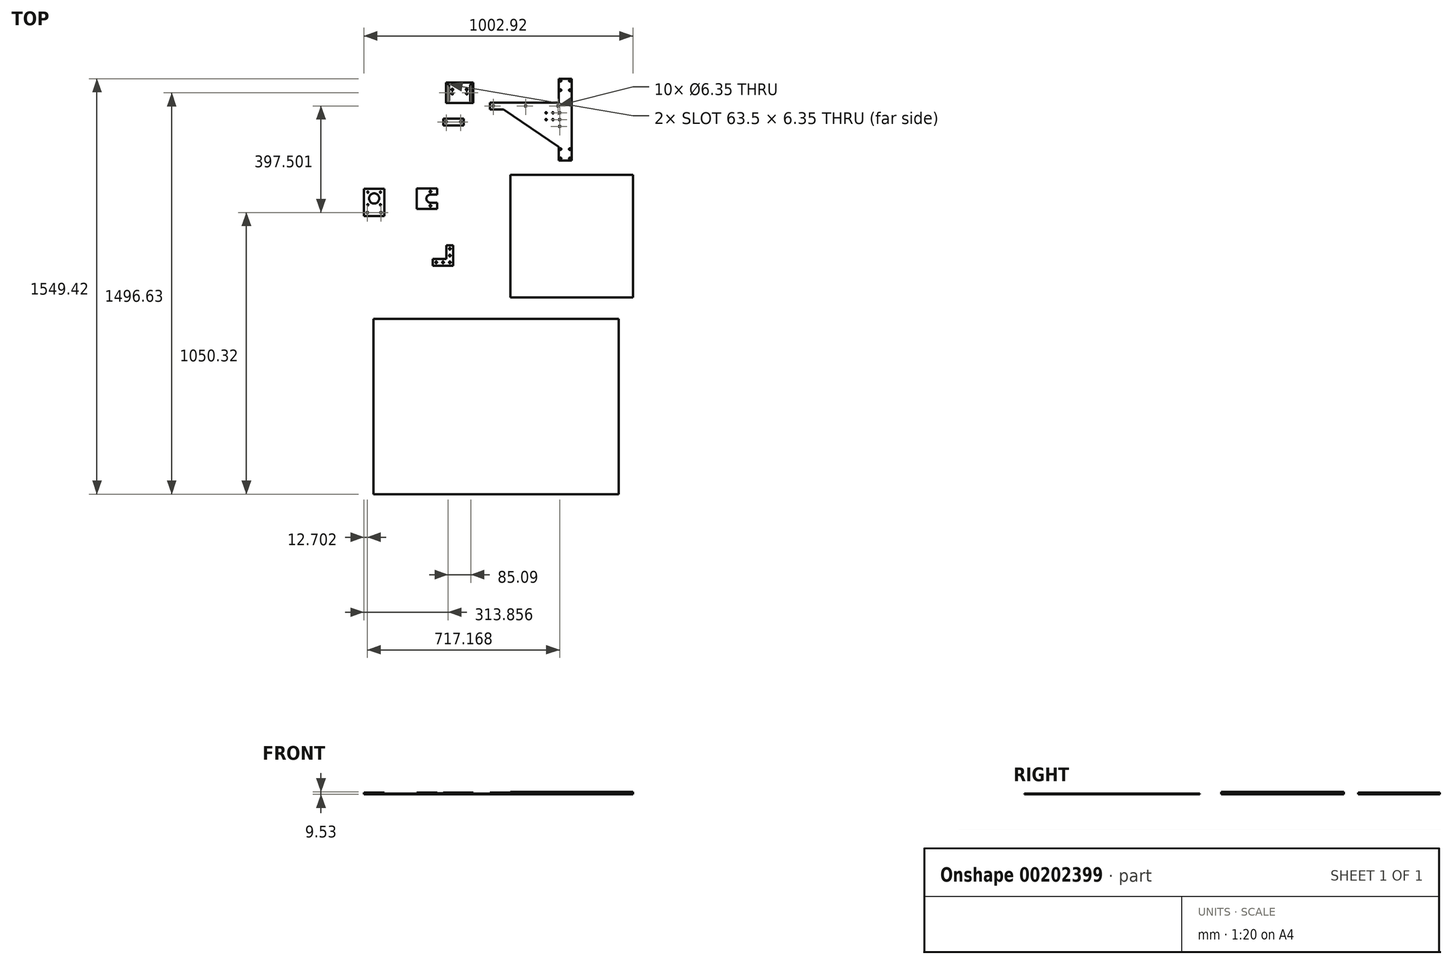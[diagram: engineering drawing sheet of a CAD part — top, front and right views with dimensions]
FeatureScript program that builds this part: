
annotation { "Feature Type Name" : "Feature", "Feature Type Description" : "" }
export const myFeature = defineFeature(function(context is Context, id is Id, definition is map)
    precondition{}
    {
        {
            var Q0;
            Q0=qCreatedBy(makeId("Top.planeOp"),FACE);
            var sketch = newSketch(context, id + "F0", { "sketchPlane" : qUnion([Q0])});
            skLineSegment(sketch, "E0.rect.bottom", {"start": v(228.6, 228.6) * mm, "end": v(-228.6, 228.6) * mm});
            skLineSegment(sketch, "E0.rect.top", {"start": v(228.6, -228.6) * mm, "end": v(-228.6, -228.6) * mm});
            skLineSegment(sketch, "E0.rect.left", {"start": v(228.6, 228.6) * mm, "end": v(228.6, -228.6) * mm});
            skLineSegment(sketch, "E0.rect.right", {"start": v(-228.6, 228.6) * mm, "end": v(-228.6, -228.6) * mm});
            skPoint(sketch, "E0.rect.middle", {"position": v(0, 0) * mm});
            skSolve(sketch);
        }
        {
            var Q0;
            Q0=makeQuery(id+"F0.imprint","IMPRINT",FACE,{"disambiguationData":[TD([[makeQuery(id+"F0.imprint","IMPRINT",EDGE,{"derivedFrom":sQuery(id+"F0.wireOp",EDGE,"E0.rect.bottom")}),1.0]])]});
            extrude(context, id + "F1", {"entities" : qUnion([Q0]), "depth" : 9.52 * mm});
        }
        {
            var Q0;
            Q0=qCreatedBy(makeId("Top.planeOp"),FACE);
            var sketch = newSketch(context, id + "F2", { "sketchPlane" : qUnion([Q0])});
            skLineSegment(sketch, "E1.rect.left", {"start": v(0, 281.9) * mm, "end": v(0, 586.7) * mm});
            skLineSegment(sketch, "E2", {"start": v(-47.75, 281.9) * mm, "end": v(0, 281.9) * mm});
            skLineSegment(sketch, "E3", {"start": v(-47.75, 586.7) * mm, "end": v(0, 586.7) * mm});
            skLineSegment(sketch, "E4", {"start": v(-304.8, 497.8) * mm, "end": v(-304.8, 472.4) * mm});
            skLineSegment(sketch, "E5", {"start": v(-47.75, 281.9) * mm, "end": v(-47.75, 332.7) * mm});
            skLineSegment(sketch, "E6", {"start": v(-47.75, 586.7) * mm, "end": v(-47.75, 497.8) * mm});
            skLineSegment(sketch, "E7", {"start": v(-304.8, 497.8) * mm, "end": v(-254, 497.8) * mm});
            skLineSegment(sketch, "E8", {"start": v(-254, 497.8) * mm, "end": v(-47.75, 497.8) * mm});
            skLineSegment(sketch, "E9", {"start": v(-304.8, 472.4) * mm, "end": v(-254, 472.4) * mm});
            skLineSegment(sketch, "E10", {"start": v(-254, 472.4) * mm, "end": v(-47.75, 332.7) * mm});
            skLineSegment(sketch, "E11", {"start": v(-304.8, 485.1) * mm, "end": v(0, 485.1) * mm, "construction": true});
            skLineSegment(sketch, "E12", {"start": v(-41.38, 586.7) * mm, "end": v(-41.38, 579.19) * mm, "construction": true});
            skLineSegment(sketch, "E13", {"start": v(-6.38, 586.7) * mm, "end": v(-6.38, 281.9) * mm, "construction": true});
            skLineSegment(sketch, "E14", {"start": v(-47.75, 579.19) * mm, "end": v(0, 579.19) * mm, "construction": true});
            skLineSegment(sketch, "E15", {"start": v(-47.75, 544.19) * mm, "end": v(0, 544.19) * mm, "construction": true});
            skLineSegment(sketch, "E16", {"start": v(-47.75, 324.43) * mm, "end": v(0, 324.43) * mm, "construction": true});
            skLineSegment(sketch, "E17", {"start": v(-47.75, 289.43) * mm, "end": v(-41.38, 289.43) * mm, "construction": true});
            skLineSegment(sketch, "E18", {"start": v(-41.38, 324.43) * mm, "end": v(-41.38, 289.43) * mm, "construction": true});
            skLineSegment(sketch, "E19", {"start": v(-41.38, 289.43) * mm, "end": v(-41.38, 281.9) * mm, "construction": true});
            skLineSegment(sketch, "E20", {"start": v(-41.38, 289.43) * mm, "end": v(-6.38, 289.43) * mm, "construction": true});
            skLineSegment(sketch, "E21", {"start": v(-6.38, 289.43) * mm, "end": v(0, 289.43) * mm, "construction": true});
            skLineSegment(sketch, "E22", {"start": v(-41.38, 579.19) * mm, "end": v(-41.38, 544.19) * mm, "construction": true});
            skLineSegment(sketch, "E23", {"start": v(-41.38, 544.19) * mm, "end": v(-41.38, 324.43) * mm, "construction": true});
            skPoint(sketch, "E24", {"position": v(-41.38, 306.93) * mm});
            skPoint(sketch, "E25", {"position": v(-41.38, 561.69) * mm});
            skCircle(sketch, "E26", {"center": v(-41.38, 324.43) * mm, "radius": 3.2 * mm});
            skCircle(sketch, "E27", {"center": v(-6.38, 324.43) * mm, "radius": 3.2 * mm});
            skCircle(sketch, "E28", {"center": v(-41.38, 289.43) * mm, "radius": 3.2 * mm});
            skCircle(sketch, "E29", {"center": v(-6.38, 289.43) * mm, "radius": 3.2 * mm});
            skCircle(sketch, "E30", {"center": v(-41.38, 579.19) * mm, "radius": 3.2 * mm});
            skCircle(sketch, "E31", {"center": v(-6.38, 579.19) * mm, "radius": 3.2 * mm});
            skCircle(sketch, "E32", {"center": v(-41.38, 544.19) * mm, "radius": 3.2 * mm});
            skCircle(sketch, "E33", {"center": v(-6.38, 544.19) * mm, "radius": 3.2 * mm});
            skCircle(sketch, "E34", {"center": v(-171.45, 485.1) * mm, "radius": 3.17 * mm});
            skCircle(sketch, "E35", {"center": v(-50.8, 485.1) * mm, "radius": 3.17 * mm});
            skCircle(sketch, "E36", {"center": v(-292.1, 485.1) * mm, "radius": 3.17 * mm});
            skCircle(sketch, "E37", {"center": v(-69.85, 459.7) * mm, "radius": 2.55 * mm});
            skCircle(sketch, "E38", {"center": v(-69.85, 434.3) * mm, "radius": 2.55 * mm});
            skCircle(sketch, "E39", {"center": v(-95.25, 459.7) * mm, "radius": 2.55 * mm});
            skCircle(sketch, "E40", {"center": v(-95.25, 434.3) * mm, "radius": 2.55 * mm});
            skLineSegment(sketch, "E41", {"start": v(-44.45, 608.23) * mm, "end": v(-44.45, 265.2) * mm, "construction": true});
            skCircle(sketch, "E42", {"center": v(-44.45, 459.7) * mm, "radius": 3.17 * mm});
            skCircle(sketch, "E43", {"center": v(-44.45, 434.3) * mm, "radius": 3.17 * mm});
            skCircle(sketch, "E44", {"center": v(-44.45, 408.9) * mm, "radius": 3.18 * mm});
            skSolve(sketch);
        }
        {
            var Q0;
            Q0=makeQuery(id+"F2.imprint","IMPRINT",FACE,{"disambiguationData":[TD([[makeQuery(id+"F2.imprint","IMPRINT",EDGE,{"derivedFrom":sQuery(id+"F2.wireOp",EDGE,"E1.rect.left")}),1.0]])]});
            extrude(context, id + "F3", {"entities" : qUnion([Q0]), "depth" : 6.35 * mm});
        }
        {
            var Q0;
            Q0=qCreatedBy(makeId("Top.planeOp"),FACE);
            var sketch = newSketch(context, id + "F4", { "sketchPlane" : qUnion([Q0])});
            skLineSegment(sketch, "E45", {"start": v(-517.53, -110.74) * mm, "end": v(-441.33, -110.74) * mm});
            skLineSegment(sketch, "E46", {"start": v(-441.33, -110.74) * mm, "end": v(-441.33, -34.54) * mm});
            skLineSegment(sketch, "E47", {"start": v(-441.33, -34.54) * mm, "end": v(-466.73, -34.54) * mm});
            skLineSegment(sketch, "E48", {"start": v(-466.73, -34.54) * mm, "end": v(-466.73, -85.34) * mm});
            skLineSegment(sketch, "E49", {"start": v(-466.73, -85.34) * mm, "end": v(-517.53, -85.34) * mm});
            skLineSegment(sketch, "E50", {"start": v(-517.53, -85.34) * mm, "end": v(-517.53, -110.74) * mm});
            skCircle(sketch, "E51", {"center": v(-454.03, -98.04) * mm, "radius": 3.26 * mm});
            skCircle(sketch, "E52.1.0.0", {"center": v(-454.03, -72.64) * mm, "radius": 3.26 * mm});
            skCircle(sketch, "E52.2.0.0", {"center": v(-454.03, -47.24) * mm, "radius": 3.26 * mm});
            skLineSegment(sketch, "E52.direction1", {"start": v(-454.03, -98.04) * mm, "end": v(-454.03, -72.64) * mm, "construction": true});
            skCircle(sketch, "E53.1.0.0", {"center": v(-479.43, -98.04) * mm, "radius": 3.26 * mm});
            skCircle(sketch, "E53.2.0.0", {"center": v(-504.83, -98.04) * mm, "radius": 3.26 * mm});
            skLineSegment(sketch, "E53.direction1", {"start": v(-454.03, -98.04) * mm, "end": v(-479.43, -98.04) * mm, "construction": true});
            skSolve(sketch);
        }
        {
            var Q0;
            Q0=makeQuery(id+"F4.imprint","IMPRINT",FACE,{"disambiguationData":[TD([[makeQuery(id+"F4.imprint","IMPRINT",EDGE,{"derivedFrom":sQuery(id+"F4.wireOp",EDGE,"E45")}),1.0]])]});
            extrude(context, id + "F5", {"entities" : qUnion([Q0]), "depth" : 4.78 * mm});
        }
        {
            var Q0;
            Q0=qCreatedBy(makeId("Top.planeOp"),FACE);
            var sketch = newSketch(context, id + "F6", { "sketchPlane" : qUnion([Q0])});
            skLineSegment(sketch, "E54.bottom", {"start": v(-577.32, 177.55) * mm, "end": v(-526.52, 177.55) * mm});
            skLineSegment(sketch, "E54.top", {"start": v(-577.32, 101.35) * mm, "end": v(-526.52, 101.35) * mm});
            skLineSegment(sketch, "E54.left", {"start": v(-577.32, 177.55) * mm, "end": v(-577.32, 101.35) * mm});
            skLineSegment(sketch, "E54.right", {"start": v(-526.52, 177.55) * mm, "end": v(-526.52, 154.45) * mm, "construction": true});
            skArc(sketch, "E55", {"start": v(-526.52, 154.45) * mm, "mid": v(-541.52, 139.45) * mm, "end": v(-526.52, 124.45) * mm});
            skLineSegment(sketch, "E56.trimOffspring", {"start": v(-526.52, 124.45) * mm, "end": v(-526.52, 101.35) * mm, "construction": true});
            skLineSegment(sketch, "E57", {"start": v(-526.52, 101.35) * mm, "end": v(-501.12, 101.35) * mm});
            skLineSegment(sketch, "E58", {"start": v(-501.12, 101.35) * mm, "end": v(-501.12, 124.45) * mm});
            skLineSegment(sketch, "E59", {"start": v(-501.12, 124.45) * mm, "end": v(-526.52, 124.45) * mm});
            skLineSegment(sketch, "E60", {"start": v(-526.52, 154.45) * mm, "end": v(-501.12, 154.45) * mm});
            skLineSegment(sketch, "E61", {"start": v(-501.12, 154.45) * mm, "end": v(-501.12, 177.55) * mm});
            skLineSegment(sketch, "E62", {"start": v(-501.12, 177.55) * mm, "end": v(-526.52, 177.55) * mm});
            skCircle(sketch, "E63", {"center": v(-526.52, 166) * mm, "radius": 3.3 * mm});
            skCircle(sketch, "E64", {"center": v(-526.52, 112.9) * mm, "radius": 3.3 * mm});
            skSolve(sketch);
        }
        {
            var Q0;
            Q0=makeQuery(id+"F6.imprint","IMPRINT",FACE,{"disambiguationData":[TD([[makeQuery(id+"F6.imprint","IMPRINT",EDGE,{"derivedFrom":sQuery(id+"F6.wireOp",EDGE,"E54.bottom")}),-1.0]])]});
            extrude(context, id + "F7", {"entities" : qUnion([Q0]), "depth" : 6.35 * mm});
        }
        {
            var Q0;
            Q0=qCreatedBy(makeId("Top.planeOp"),FACE);
            var sketch = newSketch(context, id + "F8", { "sketchPlane" : qUnion([Q0])});
            skLineSegment(sketch, "E65.rect.bottom", {"start": v(175.27, -962.71) * mm, "end": v(-739.13, -962.71) * mm});
            skLineSegment(sketch, "E65.rect.top", {"start": v(175.27, -308.66) * mm, "end": v(-739.13, -308.66) * mm});
            skLineSegment(sketch, "E65.rect.left", {"start": v(175.27, -962.71) * mm, "end": v(175.27, -308.66) * mm});
            skLineSegment(sketch, "E65.rect.right", {"start": v(-739.13, -962.71) * mm, "end": v(-739.13, -308.66) * mm});
            skPoint(sketch, "E65.rect.middle", {"position": v(-281.93, -635.69) * mm});
            skSolve(sketch);
        }
        {
            var Q0;
            Q0=makeQuery(id+"F8.imprint","IMPRINT",FACE,{"disambiguationData":[TD([[makeQuery(id+"F8.imprint","IMPRINT",EDGE,{"derivedFrom":sQuery(id+"F8.wireOp",EDGE,"E65.rect.bottom")}),-1.0]])]});
            extrude(context, id + "F9", {"entities" : qUnion([Q0]), "depth" : 3.17 * mm});
        }
        {
            var Q0;
            Q0=makeQuery(id+"F1.opExtrude","CAP_FACE",FACE,{"disambiguationData":[OSD([sQuery(id+"F0.wireOp",EDGE,"E0.rect.bottom"),sQuery(id+"F0.wireOp",EDGE,"E0.rect.top"),sQuery(id+"F0.wireOp",EDGE,"E0.rect.left"),sQuery(id+"F0.wireOp",EDGE,"E0.rect.right")])],"isStart":true});
            var sketch = newSketch(context, id + "F10", { "sketchPlane" : qUnion([Q0])});
            skLineSegment(sketch, "E66", {"start": v(0, 177.8) * mm, "end": v(152.4, 177.8) * mm, "construction": true});
            skLineSegment(sketch, "E67", {"start": v(76.2, 59.27) * mm, "end": v(-76.2, 59.27) * mm, "construction": true});
            skLineSegment(sketch, "E68", {"start": v(-152.4, -59.27) * mm, "end": v(152.4, -59.27) * mm, "construction": true});
            skLineSegment(sketch, "E69", {"start": v(76.2, -177.8) * mm, "end": v(-76.2, -177.8) * mm, "construction": true});
            skLineSegment(sketch, "E70", {"start": v(76.2, -177.8) * mm, "end": v(76.2, -59.27) * mm, "construction": true});
            skLineSegment(sketch, "E71", {"start": v(76.2, -59.27) * mm, "end": v(76.2, 59.27) * mm, "construction": true});
            skLineSegment(sketch, "E72", {"start": v(76.2, 59.27) * mm, "end": v(76.2, 177.8) * mm, "construction": true});
            skPoint(sketch, "E73", {"position": v(0, 177.8) * mm});
            skPoint(sketch, "E74", {"position": v(0, -59.27) * mm});
            skLineSegment(sketch, "E75", {"start": v(76.2, 177.8) * mm, "end": v(76.2, 228.6) * mm, "construction": true});
            skLineSegment(sketch, "E76", {"start": v(76.2, -177.8) * mm, "end": v(76.2, -228.6) * mm, "construction": true});
            skLineSegment(sketch, "E77", {"start": v(-152.4, 177.8) * mm, "end": v(-228.6, 177.8) * mm, "construction": true});
            skLineSegment(sketch, "E78", {"start": v(-76.2, 59.27) * mm, "end": v(-228.6, 59.27) * mm, "construction": true});
            skLineSegment(sketch, "E79", {"start": v(152.4, 177.8) * mm, "end": v(228.6, 177.8) * mm, "construction": true});
            skLineSegment(sketch, "E80", {"start": v(76.2, 59.27) * mm, "end": v(228.6, 59.27) * mm, "construction": true});
            skLineSegment(sketch, "E81", {"start": v(-152.4, 177.8) * mm, "end": v(0, 177.8) * mm, "construction": true});
            skSolve(sketch);
        }
        {
            var Q0;
            Q0=qCreatedBy(makeId("Top.planeOp"),FACE);
            var sketch = newSketch(context, id + "F11", { "sketchPlane" : qUnion([Q0])});
            skLineSegment(sketch, "E82.bottom", {"start": v(-468.72, 572.02) * mm, "end": v(-367.12, 572.02) * mm});
            skLineSegment(sketch, "E82.top", {"start": v(-468.72, 495.82) * mm, "end": v(-367.12, 495.82) * mm});
            skLineSegment(sketch, "E82.left", {"start": v(-468.72, 572.02) * mm, "end": v(-468.72, 495.82) * mm});
            skLineSegment(sketch, "E82.right", {"start": v(-367.12, 572.02) * mm, "end": v(-367.12, 495.82) * mm});
            skLineSegment(sketch, "E83.bottom", {"start": v(-478.47, 438.44) * mm, "end": v(-402.27, 438.44) * mm});
            skLineSegment(sketch, "E83.top", {"start": v(-478.47, 413.04) * mm, "end": v(-402.27, 413.04) * mm});
            skLineSegment(sketch, "E83.left", {"start": v(-478.47, 438.44) * mm, "end": v(-478.47, 413.04) * mm});
            skLineSegment(sketch, "E83.right", {"start": v(-402.27, 438.44) * mm, "end": v(-402.27, 413.04) * mm});
            skLineSegment(sketch, "E84", {"start": v(-478.47, 425.74) * mm, "end": v(-467.37, 425.74) * mm, "construction": true});
            skLineSegment(sketch, "E85", {"start": v(-468.72, 546.62) * mm, "end": v(-444.92, 546.62) * mm, "construction": true});
            skLineSegment(sketch, "E86", {"start": v(-468.72, 531.64) * mm, "end": v(-367.12, 531.64) * mm, "construction": true});
            skCircle(sketch, "E87", {"center": v(-467.37, 425.74) * mm, "radius": 3.17 * mm});
            skCircle(sketch, "E88", {"center": v(-413.37, 425.74) * mm, "radius": 3.17 * mm});
            skCircle(sketch, "E89", {"center": v(-444.92, 546.62) * mm, "radius": 3.3 * mm});
            skCircle(sketch, "E90", {"center": v(-390.92, 546.62) * mm, "radius": 3.3 * mm});
            skCircle(sketch, "E91", {"center": v(-444.92, 531.64) * mm, "radius": 3.3 * mm});
            skCircle(sketch, "E92", {"center": v(-390.92, 531.64) * mm, "radius": 3.3 * mm});
            skLineSegment(sketch, "E93", {"start": v(-463.64, 562.5) * mm, "end": v(-463.64, 505.35) * mm});
            skLineSegment(sketch, "E94", {"start": v(-457.29, 562.5) * mm, "end": v(-457.29, 505.35) * mm});
            skLineSegment(sketch, "E95", {"start": v(-417.92, 572.02) * mm, "end": v(-417.92, 495.82) * mm, "construction": true});
            skArc(sketch, "E96", {"start": v(-457.29, 505.35) * mm, "mid": v(-460.46, 502.17) * mm, "end": v(-463.64, 505.35) * mm});
            skArc(sketch, "E97", {"start": v(-463.64, 562.5) * mm, "mid": v(-460.46, 565.67) * mm, "end": v(-457.29, 562.5) * mm});
            skLineSegment(sketch, "E98.MirrorCS", {"start": v(-372.2, 562.5) * mm, "end": v(-372.2, 505.35) * mm});
            skLineSegment(sketch, "E99.MirrorCS", {"start": v(-378.55, 562.5) * mm, "end": v(-378.55, 505.35) * mm});
            skArc(sketch, "E100.MirrorCS", {"start": v(-372.2, 562.5) * mm, "mid": v(-375.37, 565.67) * mm, "end": v(-378.55, 562.5) * mm});
            skArc(sketch, "E101.MirrorCS", {"start": v(-378.55, 505.35) * mm, "mid": v(-375.37, 502.17) * mm, "end": v(-372.2, 505.35) * mm});
            skLineSegment(sketch, "E102", {"start": v(-444.92, 546.62) * mm, "end": v(-390.92, 546.62) * mm, "construction": true});
            skLineSegment(sketch, "E103", {"start": v(-390.92, 546.62) * mm, "end": v(-367.12, 546.62) * mm, "construction": true});
            skLineSegment(sketch, "E104", {"start": v(-467.37, 425.74) * mm, "end": v(-413.37, 425.74) * mm, "construction": true});
            skLineSegment(sketch, "E105", {"start": v(-413.37, 425.74) * mm, "end": v(-402.27, 425.74) * mm, "construction": true});
            skSolve(sketch);
        }
        {
            var Q0;
            Q0=makeQuery(id+"F11.imprint","IMPRINT",FACE,{"disambiguationData":[TD([[makeQuery(id+"F11.imprint","IMPRINT",EDGE,{"derivedFrom":sQuery(id+"F11.wireOp",EDGE,"E82.bottom")}),-1.0]])]});
            var Q1;
            Q1=makeQuery(id+"F11.imprint","IMPRINT",FACE,{"disambiguationData":[TD([[makeQuery(id+"F11.imprint","IMPRINT",EDGE,{"derivedFrom":sQuery(id+"F11.wireOp",EDGE,"E83.bottom")}),-1.0]])]});
            extrude(context, id + "F12", {"entities" : qUnion([Q0, Q1]), "depth" : 6.35 * mm});
        }
        {
            var Q0;
            Q0=qCreatedBy(makeId("Top.planeOp"),FACE);
            var sketch = newSketch(context, id + "F13", { "sketchPlane" : qUnion([Q0])});
            skLineSegment(sketch, "E106.rect.bottom", {"start": v(-698.12, 74.9) * mm, "end": v(-774.32, 74.9) * mm});
            skLineSegment(sketch, "E106.rect.top", {"start": v(-698.12, 176.5) * mm, "end": v(-774.32, 176.5) * mm});
            skLineSegment(sketch, "E106.rect.left", {"start": v(-698.12, 74.9) * mm, "end": v(-698.12, 176.5) * mm});
            skLineSegment(sketch, "E106.rect.right", {"start": v(-774.32, 74.9) * mm, "end": v(-774.32, 176.5) * mm});
            skPoint(sketch, "E106.rect.middle", {"position": v(-736.22, 125.7) * mm});
            skCircle(sketch, "E107", {"center": v(-759.72, 163.8) * mm, "radius": 2.5 * mm});
            skCircle(sketch, "E108", {"center": v(-712.72, 163.8) * mm, "radius": 2.5 * mm});
            skCircle(sketch, "E109", {"center": v(-759.72, 116.8) * mm, "radius": 2.5 * mm});
            skCircle(sketch, "E110", {"center": v(-712.72, 116.8) * mm, "radius": 2.5 * mm});
            skLineSegment(sketch, "E111", {"start": v(-712.72, 163.8) * mm, "end": v(-712.72, 116.8) * mm, "construction": true});
            skLineSegment(sketch, "E112", {"start": v(-712.72, 116.8) * mm, "end": v(-759.72, 116.8) * mm, "construction": true});
            skLineSegment(sketch, "E113", {"start": v(-759.72, 116.8) * mm, "end": v(-759.72, 163.8) * mm, "construction": true});
            skLineSegment(sketch, "E114", {"start": v(-759.72, 163.8) * mm, "end": v(-712.72, 163.8) * mm, "construction": true});
            skPoint(sketch, "E115", {"position": v(-736.22, 163.8) * mm});
            skPoint(sketch, "E116", {"position": v(-712.72, 140.3) * mm});
            skCircle(sketch, "E117", {"center": v(-761.62, 87.6) * mm, "radius": 3.18 * mm});
            skCircle(sketch, "E118", {"center": v(-710.82, 87.6) * mm, "radius": 3.18 * mm});
            skLineSegment(sketch, "E119", {"start": v(-759.72, 163.8) * mm, "end": v(-712.72, 116.8) * mm, "construction": true});
            skCircle(sketch, "E120", {"center": v(-736.22, 140.3) * mm, "radius": 19.05 * mm});
            skSolve(sketch);
        }
        {
            var Q0;
            Q0=makeQuery(id+"F13.imprint","IMPRINT",FACE,{"disambiguationData":[TD([[makeQuery(id+"F13.imprint","IMPRINT",EDGE,{"derivedFrom":sQuery(id+"F13.wireOp",EDGE,"E106.rect.bottom")}),-1.0]])]});
            extrude(context, id + "F14", {"entities" : qUnion([Q0]), "depth" : 6.35 * mm});
        }
    });
